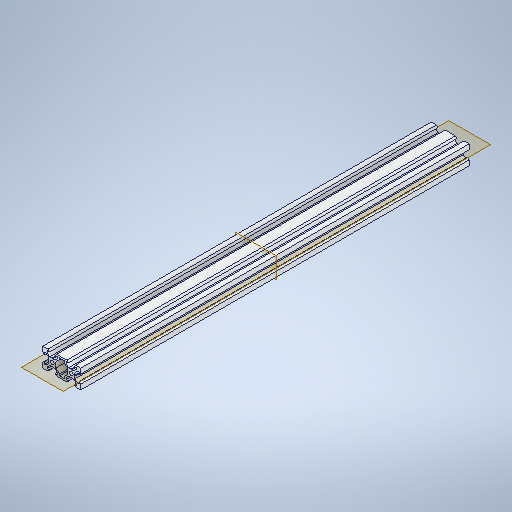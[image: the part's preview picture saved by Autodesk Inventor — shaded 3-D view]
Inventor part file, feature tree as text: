
AUTODESK INVENTOR PART (.ipt)
format: ipt  version: 2025.2 (Build 292293000, 293)  size: 388,608 bytes
history: native  units: in
note: dims shown in document units (in); Inventor stores cm internally (conversion verified against a paired STEP export)
features: plane x2, extrude x1, sketch x1, other x1
ambient origin geometry x8: Origin, YZ Plane, XZ Plane, XY Plane, X Axis, Y Axis, Z Axis, Center Point
bodies: Solid1 (feature_tree)
feature tree (5):
  extrude  "Extrusion1"  [1 undecoded]
  plane  "Work Plane1"
  plane  "Work Plane2"
  sketch  "Sketch1"  dims[d0=3.5433in d1=0.0in d2=-8.0709in]
  other  "Boss-Extrude1"
note: 1 required parameter value undecoded (feature->parameter linkage not recoverable at this tier; creation-order binding heuristic only, values carry confidence <= 0.55)
